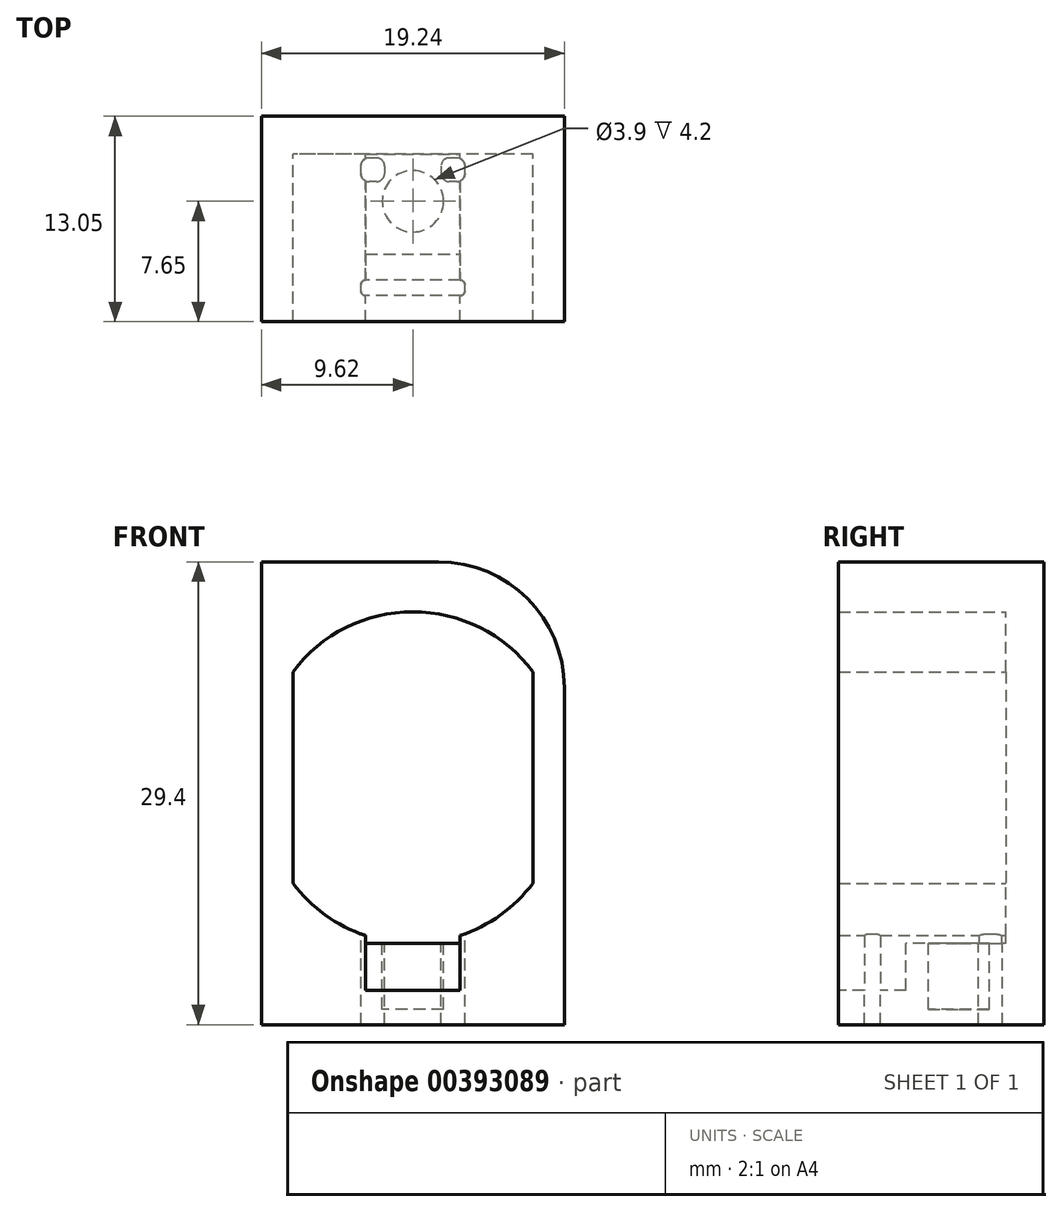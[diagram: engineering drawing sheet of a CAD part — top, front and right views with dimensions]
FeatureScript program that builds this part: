
annotation { "Feature Type Name" : "Feature", "Feature Type Description" : "" }
export const myFeature = defineFeature(function(context is Context, id is Id, definition is map)
    precondition{}
    {
        {
            var Q0;
            Q0=qCreatedBy(makeId("Front.planeOp"),FACE);
            var sketch = newSketch(context, id + "F0", { "sketchPlane" : qUnion([Q0])});
            skCircle(sketch, "E0", {"center": v(0, 0) * mm, "radius": 9.53 * mm});
            skSolve(sketch);
        }
        {
            var Q0;
            Q0=qCreatedBy(makeId("Front.planeOp"),FACE);
            var sketch = newSketch(context, id + "F1", { "sketchPlane" : qUnion([Q0])});
            skLineSegment(sketch, "E1.bottom", {"start": v(9.62, 12.7) * mm, "end": v(7.62, 12.7) * mm});
            skLineSegment(sketch, "E1.top", {"start": v(9.62, -1) * mm, "end": v(7.62, -1) * mm});
            skLineSegment(sketch, "E1.left", {"start": v(9.62, 12.7) * mm, "end": v(9.62, -1) * mm});
            skLineSegment(sketch, "E1.right", {"start": v(7.62, 12.7) * mm, "end": v(7.62, -1) * mm});
            skLineSegment(sketch, "E2.bottom", {"start": v(-9.62, 12.7) * mm, "end": v(-7.62, 12.7) * mm});
            skLineSegment(sketch, "E2.top", {"start": v(-9.62, -1) * mm, "end": v(-7.62, -1) * mm});
            skLineSegment(sketch, "E2.left", {"start": v(-9.62, 12.7) * mm, "end": v(-9.62, -1) * mm});
            skLineSegment(sketch, "E2.right", {"start": v(-7.62, 12.7) * mm, "end": v(-7.62, -1) * mm});
            skLineSegment(sketch, "E3", {"start": v(0, 12.7) * mm, "end": v(0, -12.7) * mm, "construction": true});
            skLineSegment(sketch, "E4.bottom", {"start": v(-7.62, 12.7) * mm, "end": v(7.62, 12.7) * mm});
            skLineSegment(sketch, "E4.left", {"start": v(-7.62, 12.7) * mm, "end": v(-7.62, 4.7) * mm});
            skLineSegment(sketch, "E4.right", {"start": v(7.62, 12.7) * mm, "end": v(7.62, 4.7) * mm});
            skArc(sketch, "E5.trimOffspring", {"start": v(7.62, 5.72) * mm, "mid": v(0, 9.53) * mm, "end": v(-7.62, 5.72) * mm});
            skSolve(sketch);
        }
        {
            var Q0;
            Q0=qSketchRegion(id+"F1",true);
            extrude(context, id + "F2", {"entities" : qUnion([Q0]), "depth" : 10.65 * mm});
        }
        {
            var Q0;
            Q0=makeQuery(id+"F2.opExtrude","SWEPT_BODY",BODY,{"disambiguationData":[OSD([sQuery(id+"F1.wireOp",EDGE,"E1.bottom"),sQuery(id+"F1.wireOp",EDGE,"E1.top"),sQuery(id+"F1.wireOp",EDGE,"E1.left"),sQuery(id+"F1.wireOp",EDGE,"E1.right"),sQuery(id+"F1.wireOp",EDGE,"E2.bottom"),sQuery(id+"F1.wireOp",EDGE,"E2.top"),sQuery(id+"F1.wireOp",EDGE,"E2.left"),sQuery(id+"F1.wireOp",EDGE,"E2.right"),sQuery(id+"F1.wireOp",EDGE,"E4.bottom"),sQuery(id+"F1.wireOp",EDGE,"E4.left"),sQuery(id+"F1.wireOp",EDGE,"E4.right"),sQuery(id+"F1.wireOp",EDGE,"E5.trimOffspring")])]});
            var Q1;
            Q1=makeQuery(id+"F2.opExtrude","SWEPT_FACE",FACE,{"disambiguationData":[OSD([sQuery(id+"F1.wireOp",EDGE,"E2.top")])]});
            mirror(context, id + "F3", {"operationType" : NewBodyOperationType.ADD, "entities" : qUnion([Q0]), "mirrorPlane" : qUnion([Q1])});
        }
        {
            var Q0;
            {var subQ0=makeQuery(id+"F2.opExtrude","CAP_FACE",FACE,{"disambiguationData":[OSD([sQuery(id+"F1.wireOp",EDGE,"E1.bottom"),sQuery(id+"F1.wireOp",EDGE,"E1.top"),sQuery(id+"F1.wireOp",EDGE,"E1.left"),sQuery(id+"F1.wireOp",EDGE,"E1.right"),sQuery(id+"F1.wireOp",EDGE,"E2.bottom"),sQuery(id+"F1.wireOp",EDGE,"E2.top"),sQuery(id+"F1.wireOp",EDGE,"E2.left"),sQuery(id+"F1.wireOp",EDGE,"E2.right"),sQuery(id+"F1.wireOp",EDGE,"E4.bottom"),sQuery(id+"F1.wireOp",EDGE,"E4.left"),sQuery(id+"F1.wireOp",EDGE,"E4.right"),sQuery(id+"F1.wireOp",EDGE,"E5.trimOffspring")])],"isStart":true});Q0=makeQuery(id+"F3.boolean.opBoolean","MERGE",FACE,{"derivedFrom":[subQ0,makeQuery(id+"F3.opPattern","COPY",FACE,{"derivedFrom":subQ0,"instanceName":"1"})]});}
            var sketch = newSketch(context, id + "F4", { "sketchPlane" : qUnion([Q0])});
            skLineSegment(sketch, "E6.bottom", {"start": v(-9.62, 12.7) * mm, "end": v(9.62, 12.7) * mm});
            skLineSegment(sketch, "E6.top", {"start": v(-9.62, -14.7) * mm, "end": v(9.62, -14.7) * mm});
            skLineSegment(sketch, "E6.left", {"start": v(-9.62, 12.7) * mm, "end": v(-9.62, -14.7) * mm});
            skLineSegment(sketch, "E6.right", {"start": v(9.62, 12.7) * mm, "end": v(9.62, -14.7) * mm});
            skSolve(sketch);
        }
        {
            var Q0;
            Q0=qSketchRegion(id+"F4",true);
            extrude(context, id + "F5", {"entities" : qUnion([Q0]), "operationType" : NewBodyOperationType.ADD, "depth" : 2.4 * mm});
        }
        {
            var Q0;
            {var subQ0=makeQuery(id+"F2.opExtrude","CAP_FACE",FACE,{"disambiguationData":[OSD([sQuery(id+"F1.wireOp",EDGE,"E1.bottom"),sQuery(id+"F1.wireOp",EDGE,"E1.top"),sQuery(id+"F1.wireOp",EDGE,"E1.left"),sQuery(id+"F1.wireOp",EDGE,"E1.right"),sQuery(id+"F1.wireOp",EDGE,"E2.bottom"),sQuery(id+"F1.wireOp",EDGE,"E2.top"),sQuery(id+"F1.wireOp",EDGE,"E2.left"),sQuery(id+"F1.wireOp",EDGE,"E2.right"),sQuery(id+"F1.wireOp",EDGE,"E4.bottom"),sQuery(id+"F1.wireOp",EDGE,"E4.left"),sQuery(id+"F1.wireOp",EDGE,"E4.right"),sQuery(id+"F1.wireOp",EDGE,"E5.trimOffspring")])],"isStart":false});Q0=makeQuery(id+"F3.boolean.opBoolean","MERGE",FACE,{"derivedFrom":[subQ0,makeQuery(id+"F3.opPattern","COPY",FACE,{"derivedFrom":subQ0,"instanceName":"1"})]});}
            var sketch = newSketch(context, id + "F6", { "sketchPlane" : qUnion([Q0])});
            skLineSegment(sketch, "E7.top", {"start": v(3, -10.86) * mm, "end": v(-3, -10.86) * mm});
            skLineSegment(sketch, "E7.left", {"start": v(3, -11.52) * mm, "end": v(3, -10.86) * mm});
            skLineSegment(sketch, "E7.right", {"start": v(-3, -11.52) * mm, "end": v(-3, -10.86) * mm});
            skPoint(sketch, "E7.middle", {"position": v(0, -11.52) * mm});
            skLineSegment(sketch, "E8", {"start": v(-3, -11.52) * mm, "end": v(3, -11.52) * mm});
            skSolve(sketch);
        }
        {
            var Q0;
            Q0=qSketchRegion(id+"F6",true);
            var Q1;
            Q1=makeQuery(id+"F5.opExtrude","CAP_FACE",FACE,{"disambiguationData":[OSD([sQuery(id+"F4.wireOp",EDGE,"E6.bottom"),sQuery(id+"F4.wireOp",EDGE,"E6.top"),sQuery(id+"F4.wireOp",EDGE,"E6.left"),sQuery(id+"F4.wireOp",EDGE,"E6.right")])],"isStart":true});
            extrude(context, id + "F7", {"entities" : qUnion([Q0]), "operationType" : NewBodyOperationType.REMOVE, "endBound" : BoundingType.UP_TO_SURFACE, "oppositeDirection" : true, "endBoundEntityFace" : qUnion([Q1]), "depth" : 10.65 * mm});
        }
        {
            var Q0;
            Q0=makeQuery(id+"F5.boolean.opBoolean","MERGE",FACE,{"derivedFrom":[makeQuery(id+"F3.opPattern","COPY",FACE,{"derivedFrom":makeQuery(id+"F2.opExtrude","SWEPT_FACE",FACE,{"disambiguationData":[OSD([sQuery(id+"F1.wireOp",EDGE,"E1.bottom"),sQuery(id+"F1.wireOp",EDGE,"E2.bottom"),sQuery(id+"F1.wireOp",EDGE,"E4.bottom")])]}),"instanceName":"1"}),makeQuery(id+"F5.opExtrude","SWEPT_FACE",FACE,{"disambiguationData":[OSD([sQuery(id+"F4.wireOp",EDGE,"E6.top")])]})]});
            var sketch = newSketch(context, id + "F8", { "sketchPlane" : qUnion([Q0])});
            skLineSegment(sketch, "E9.bottom", {"start": v(-9.62, 10.65) * mm, "end": v(9.62, 10.65) * mm});
            skLineSegment(sketch, "E9.top", {"start": v(-9.62, -2.4) * mm, "end": v(9.62, -2.4) * mm});
            skLineSegment(sketch, "E9.left", {"start": v(-9.62, 10.65) * mm, "end": v(-9.62, -2.4) * mm});
            skLineSegment(sketch, "E9.right", {"start": v(9.62, 10.65) * mm, "end": v(9.62, -2.4) * mm});
            skSolve(sketch);
        }
        {
            var Q0;
            Q0=qSketchRegion(id+"F8",true);
            extrude(context, id + "F9", {"entities" : qUnion([Q0]), "operationType" : NewBodyOperationType.ADD, "depth" : 2 * mm});
        }
        {
            var Q0;
            Q0=makeQuery(id+"F7.boolean.opBoolean","COPY",FACE,{"derivedFrom":makeQuery(id+"F7.opExtrude","SWEPT_FACE",FACE,{"disambiguationData":[OSD([sQuery(id+"F6.wireOp",EDGE,"E8")])]})});
            var sketch = newSketch(context, id + "F10", { "sketchPlane" : qUnion([Q0])});
            skCircle(sketch, "E10", {"center": v(0, -3) * mm, "radius": 1.95 * mm});
            skPoint(sketch, "E10.centerSnap0", {"position": v(0, 0) * mm});
            skSolve(sketch);
        }
        {
            var Q0;
            Q0=qSketchRegion(id+"F10",true);
            extrude(context, id + "F11", {"entities" : qUnion([Q0]), "operationType" : NewBodyOperationType.REMOVE, "oppositeDirection" : true, "depth" : 4.2 * mm});
        }
        {
            var Q0;
            Q0=makeQuery(id+"F7.boolean.opBoolean","COPY",FACE,{"derivedFrom":makeQuery(id+"F7.opExtrude","SWEPT_FACE",FACE,{"disambiguationData":[OSD([sQuery(id+"F6.wireOp",EDGE,"E8")])]})});
            var sketch = newSketch(context, id + "F12", { "sketchPlane" : qUnion([Q0])});
            skLineSegment(sketch, "E11.bottom", {"start": v(-3, -10.65) * mm, "end": v(3, -10.65) * mm});
            skLineSegment(sketch, "E11.top", {"start": v(-3, -6.35) * mm, "end": v(3, -6.35) * mm});
            skLineSegment(sketch, "E11.left", {"start": v(-3, -10.65) * mm, "end": v(-3, -6.35) * mm});
            skLineSegment(sketch, "E11.right", {"start": v(3, -10.65) * mm, "end": v(3, -6.35) * mm});
            skPoint(sketch, "E11.middle", {"position": v(0, -8.5) * mm});
            skPoint(sketch, "E11.middle.positionSnap0", {"position": v(0, -10.65) * mm});
            skPoint(sketch, "E11.centerSnap0", {"position": v(0, -10.65) * mm});
            skSolve(sketch);
        }
        {
            var Q0;
            Q0=makeQuery(id+"F12.imprint","IMPRINT",FACE,{"disambiguationData":[TD([[makeQuery(id+"F12.imprint","IMPRINT",EDGE,{"derivedFrom":sQuery(id+"F12.wireOp",EDGE,"E11.bottom")}),1.0]])]});
            extrude(context, id + "F13", {"entities" : qUnion([Q0]), "operationType" : NewBodyOperationType.REMOVE, "oppositeDirection" : true, "depth" : 3 * mm});
        }
        {
            var Q0;
            Q0=makeQuery(id+"F5.boolean.opBoolean","MERGE",EDGE,{"derivedFrom":[makeQuery(id+"F2.opExtrude","SWEPT_EDGE",EDGE,{"disambiguationData":[OSD([sQuery(id+"F1.wireOp",EDGE,"E1.bottom"),sQuery(id+"F1.wireOp",EDGE,"E1.left")])]}),makeQuery(id+"F5.opExtrude","SWEPT_EDGE",EDGE,{"disambiguationData":[OSD([sQuery(id+"F4.wireOp",EDGE,"E6.bottom"),sQuery(id+"F4.wireOp",EDGE,"E6.left")])]})]});
            fillet(context, id + "F14", {"entities" : qUnion([Q0]), "radius" : 8 * mm, "tangentPropagation" : true, "allowEdgeOverflow" : false});
        }
        {
            var Q0;
            Q0=makeQuery(id+"F13.boolean.opBoolean","COPY",FACE,{"derivedFrom":makeQuery(id+"F13.opExtrude","CAP_FACE",FACE,{"disambiguationData":[OSD([sQuery(id+"F12.wireOp",EDGE,"E11.bottom"),sQuery(id+"F12.wireOp",EDGE,"E11.top"),sQuery(id+"F12.wireOp",EDGE,"E11.left"),sQuery(id+"F12.wireOp",EDGE,"E11.right")])],"isStart":false})});
            var sketch = newSketch(context, id + "F15", { "sketchPlane" : qUnion([Q0])});
            skLineSegment(sketch, "E12.bottom", {"start": v(-3.3, -8) * mm, "end": v(3.3, -8) * mm});
            skLineSegment(sketch, "E12.top", {"start": v(-3.3, -9) * mm, "end": v(3.3, -9) * mm});
            skLineSegment(sketch, "E12.left", {"start": v(-3.3, -8) * mm, "end": v(-3.3, -9) * mm});
            skLineSegment(sketch, "E12.right", {"start": v(3.3, -8) * mm, "end": v(3.3, -9) * mm});
            skPoint(sketch, "E12.middle", {"position": v(0, -8.5) * mm});
            skPoint(sketch, "E12.middle.positionSnap0", {"position": v(0, -10.65) * mm});
            skPoint(sketch, "E12.middle.positionSnap1", {"position": v(3, -8.5) * mm});
            skPoint(sketch, "E12.centerSnap0", {"position": v(0, -10.65) * mm});
            skPoint(sketch, "E12.centerSnap1", {"position": v(3, -8.5) * mm});
            skSolve(sketch);
        }
        {
            var Q0;
            Q0=qSketchRegion(id+"F15",true);
            extrude(context, id + "F16", {"entities" : qUnion([Q0]), "operationType" : NewBodyOperationType.REMOVE, "oppositeDirection" : true, "depth" : 8 * mm, "hasSecondDirection" : true, "secondDirectionOppositeDirection" : false, "secondDirectionDepth" : 8 * mm});
        }
        {
            var Q0;
            Q0=makeQuery(id+"F16.boolean.opBoolean","COPY",EDGE,{"derivedFrom":makeQuery(id+"F16.opExtrude","SWEPT_EDGE",EDGE,{"disambiguationData":[OSD([sQuery(id+"F15.wireOp",EDGE,"E12.bottom"),sQuery(id+"F15.wireOp",EDGE,"E12.right")])]})});
            var Q1;
            Q1=makeQuery(id+"F16.boolean.opBoolean","COPY",EDGE,{"derivedFrom":makeQuery(id+"F16.opExtrude","SWEPT_EDGE",EDGE,{"disambiguationData":[OSD([sQuery(id+"F15.wireOp",EDGE,"E12.bottom"),sQuery(id+"F15.wireOp",EDGE,"E12.left")])]})});
            var Q2;
            Q2=makeQuery(id+"F16.boolean.opBoolean","COPY",EDGE,{"derivedFrom":makeQuery(id+"F16.opExtrude","SWEPT_EDGE",EDGE,{"disambiguationData":[OSD([sQuery(id+"F15.wireOp",EDGE,"E12.top"),sQuery(id+"F15.wireOp",EDGE,"E12.left")])]})});
            var Q3;
            Q3=makeQuery(id+"F16.boolean.opBoolean","COPY",EDGE,{"derivedFrom":makeQuery(id+"F16.opExtrude","SWEPT_EDGE",EDGE,{"disambiguationData":[OSD([sQuery(id+"F15.wireOp",EDGE,"E12.top"),sQuery(id+"F15.wireOp",EDGE,"E12.right")])]})});
            fillet(context, id + "F17", {"entities" : qUnion([Q0, Q1, Q2, Q3]), "radius" : .3 * mm, "tangentPropagation" : true, "allowEdgeOverflow" : false});
        }
        {
            var Q0;
            Q0=makeQuery(id+"F7.boolean.opBoolean","COPY",FACE,{"derivedFrom":makeQuery(id+"F7.opExtrude","SWEPT_FACE",FACE,{"disambiguationData":[OSD([sQuery(id+"F6.wireOp",EDGE,"E8")])]})});
            var sketch = newSketch(context, id + "F18", { "sketchPlane" : qUnion([Q0])});
            skLineSegment(sketch, "E13.bottom", {"start": v(3.3, -1.75) * mm, "end": v(1.8, -1.75) * mm});
            skLineSegment(sketch, "E13.top", {"start": v(3.3, -0.25) * mm, "end": v(1.8, -0.25) * mm});
            skLineSegment(sketch, "E13.left", {"start": v(3.3, -1.75) * mm, "end": v(3.3, -0.25) * mm});
            skLineSegment(sketch, "E13.right", {"start": v(-3.3, -1.75) * mm, "end": v(-3.3, -0.25) * mm});
            skPoint(sketch, "E13.middle", {"position": v(0, -1) * mm});
            skPoint(sketch, "E13.middle.positionSnap0", {"position": v(0, 0) * mm});
            skPoint(sketch, "E13.centerSnap0", {"position": v(0, 0) * mm});
            skLineSegment(sketch, "E14", {"start": v(-1.8, -0.25) * mm, "end": v(-1.8, -1.75) * mm});
            skLineSegment(sketch, "E15", {"start": v(1.8, -0.25) * mm, "end": v(1.8, -1.75) * mm});
            skLineSegment(sketch, "E16.trimOffspring", {"start": v(-1.8, -0.25) * mm, "end": v(-3.3, -0.25) * mm});
            skLineSegment(sketch, "E17.trimOffspring", {"start": v(-1.8, -1.75) * mm, "end": v(-3.3, -1.75) * mm});
            skSolve(sketch);
        }
        {
            var Q0;
            Q0=qSketchRegion(id+"F18",true);
            extrude(context, id + "F19", {"entities" : qUnion([Q0]), "operationType" : NewBodyOperationType.REMOVE, "endBound" : BoundingType.UP_TO_NEXT, "oppositeDirection" : true, "depth" : 25.4 * mm, "hasSecondDirection" : true, "secondDirectionOppositeDirection" : false, "secondDirectionDepth" : 1 * mm});
        }
        {
            var Q0;
            Q0=makeQuery(id+"F19.boolean.opBoolean","COPY",EDGE,{"derivedFrom":makeQuery(id+"F19.opExtrude","SWEPT_EDGE",EDGE,{"disambiguationData":[OSD([sQuery(id+"F18.wireOp",EDGE,"E13.top"),sQuery(id+"F18.wireOp",EDGE,"E13.left")])]})});
            var Q1;
            Q1=makeQuery(id+"F19.boolean.opBoolean","COPY",EDGE,{"derivedFrom":makeQuery(id+"F19.opExtrude","SWEPT_EDGE",EDGE,{"disambiguationData":[OSD([sQuery(id+"F18.wireOp",EDGE,"E13.bottom"),sQuery(id+"F18.wireOp",EDGE,"E13.left")])]})});
            var Q2;
            Q2=makeQuery(id+"F19.boolean.opBoolean","COPY",EDGE,{"derivedFrom":makeQuery(id+"F19.opExtrude","SWEPT_EDGE",EDGE,{"disambiguationData":[OSD([sQuery(id+"F18.wireOp",EDGE,"E13.bottom"),sQuery(id+"F18.wireOp",EDGE,"E15")])]})});
            var Q3;
            Q3=makeQuery(id+"F19.boolean.opBoolean","COPY",EDGE,{"derivedFrom":makeQuery(id+"F19.opExtrude","SWEPT_EDGE",EDGE,{"disambiguationData":[OSD([sQuery(id+"F18.wireOp",EDGE,"E13.top"),sQuery(id+"F18.wireOp",EDGE,"E15")])]})});
            var Q4;
            Q4=makeQuery(id+"F19.boolean.opBoolean","COPY",EDGE,{"derivedFrom":makeQuery(id+"F19.opExtrude","SWEPT_EDGE",EDGE,{"disambiguationData":[OSD([sQuery(id+"F18.wireOp",EDGE,"E13.right"),sQuery(id+"F18.wireOp",EDGE,"E16.trimOffspring")])]})});
            var Q5;
            Q5=makeQuery(id+"F19.boolean.opBoolean","COPY",EDGE,{"derivedFrom":makeQuery(id+"F19.opExtrude","SWEPT_EDGE",EDGE,{"disambiguationData":[OSD([sQuery(id+"F18.wireOp",EDGE,"E14"),sQuery(id+"F18.wireOp",EDGE,"E16.trimOffspring")])]})});
            var Q6;
            Q6=makeQuery(id+"F19.boolean.opBoolean","COPY",EDGE,{"derivedFrom":makeQuery(id+"F19.opExtrude","SWEPT_EDGE",EDGE,{"disambiguationData":[OSD([sQuery(id+"F18.wireOp",EDGE,"E14"),sQuery(id+"F18.wireOp",EDGE,"E17.trimOffspring")])]})});
            var Q7;
            Q7=makeQuery(id+"F19.boolean.opBoolean","COPY",EDGE,{"derivedFrom":makeQuery(id+"F19.opExtrude","SWEPT_EDGE",EDGE,{"disambiguationData":[OSD([sQuery(id+"F18.wireOp",EDGE,"E13.right"),sQuery(id+"F18.wireOp",EDGE,"E17.trimOffspring")])]})});
            fillet(context, id + "F20", {"entities" : qUnion([Q0, Q1, Q2, Q3, Q4, Q5, Q6, Q7]), "radius" : .5 * mm, "tangentPropagation" : true, "allowEdgeOverflow" : false});
        }
    });
